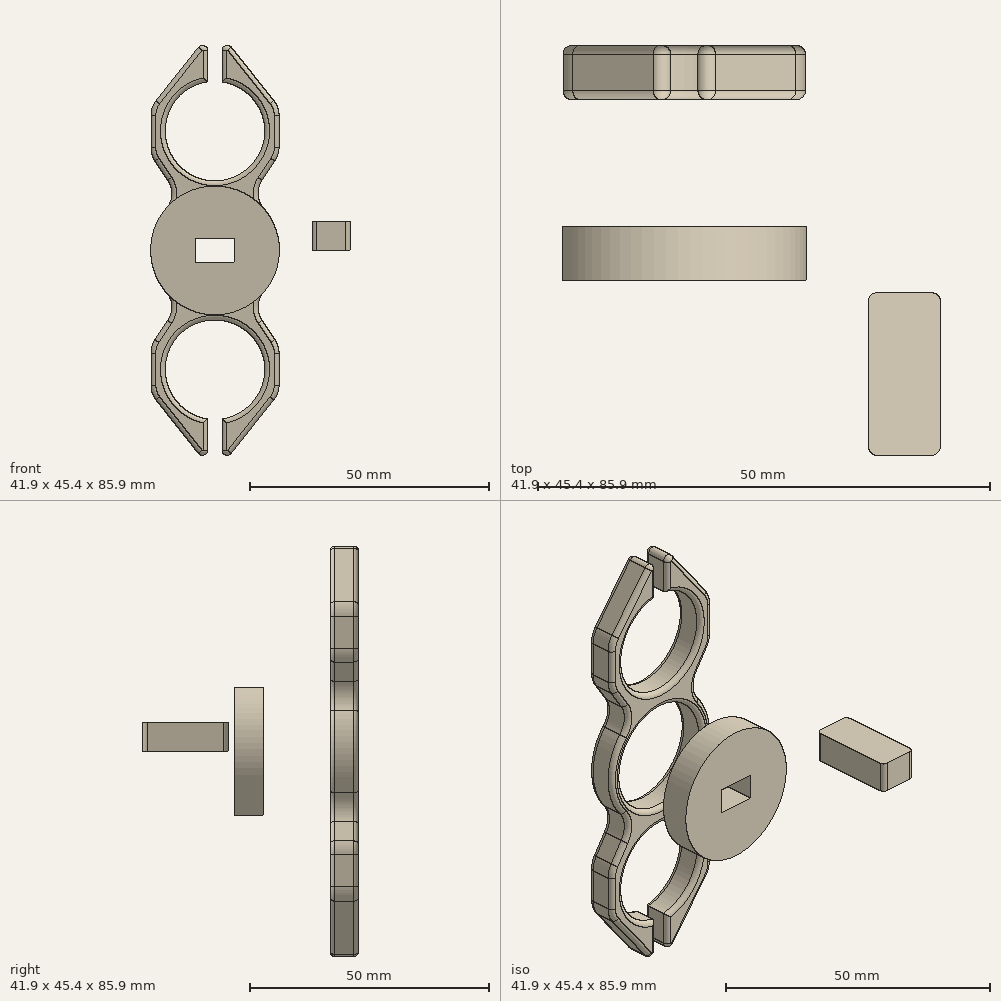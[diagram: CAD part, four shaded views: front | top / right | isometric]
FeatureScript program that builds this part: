
annotation { "Feature Type Name" : "Feature", "Feature Type Description" : "" }
export const myFeature = defineFeature(function(context is Context, id is Id, definition is map)
    precondition{}
    {
        {
            var Q0;
            Q0=qCreatedBy(makeId("Front.planeOp"),FACE);
            var sketch = newSketch(context, id + "F0", { "sketchPlane" : qUnion([Q0])});
            skCircle(sketch, "E0", {"center": v(0, 0) * mm, "radius": 10.93 * mm});
            skLineSegment(sketch, "E1", {"start": v(0, 0) * mm, "end": v(0, 25) * mm, "construction": true});
            skArc(sketch, "E2", {"start": v(-1.5, 35.32) * mm, "mid": v(0, 14.58) * mm, "end": v(1.5, 35.32) * mm});
            skArc(sketch, "E3.1.0", {"start": v(1.5, -35.32) * mm, "mid": v(0, -14.58) * mm, "end": v(-1.5, -35.32) * mm});
            skLineSegment(sketch, "E4.left", {"start": v(1.5, -41.86) * mm, "end": v(1.5, -35.32) * mm});
            skLineSegment(sketch, "E4.right", {"start": v(-1.5, -41.86) * mm, "end": v(-1.5, -35.32) * mm});
            skLineSegment(sketch, "E5.left", {"start": v(13.42, -28.26) * mm, "end": v(13.42, -21.51) * mm});
            skLineSegment(sketch, "E5.right", {"start": v(-13.42, -28.26) * mm, "end": v(-13.42, -21.51) * mm});
            skLineSegment(sketch, "E6.left", {"start": v(13.42, 21.51) * mm, "end": v(13.42, 28.26) * mm});
            skLineSegment(sketch, "E6.right", {"start": v(-13.42, 21.51) * mm, "end": v(-13.42, 28.26) * mm});
            skLineSegment(sketch, "E7", {"start": v(12.33, 31.37) * mm, "end": v(3.45, 42.54) * mm});
            skLineSegment(sketch, "E8", {"start": v(-3.45, 42.54) * mm, "end": v(-12.33, 31.37) * mm});
            skArc(sketch, "E9", {"start": v(10.23, -8.68) * mm, "mid": v(13.42, 0) * mm, "end": v(10.23, 8.68) * mm});
            skLineSegment(sketch, "E10", {"start": v(12.33, -31.37) * mm, "end": v(3.45, -42.54) * mm});
            skLineSegment(sketch, "E11", {"start": v(-3.45, -42.54) * mm, "end": v(-12.33, -31.37) * mm});
            skLineSegment(sketch, "E12", {"start": v(12.58, -18.74) * mm, "end": v(9.88, -14.7) * mm});
            skLineSegment(sketch, "E13", {"start": v(-9.88, -14.7) * mm, "end": v(-12.58, -18.74) * mm});
            skLineSegment(sketch, "E14", {"start": v(12.58, 18.74) * mm, "end": v(9.88, 14.7) * mm});
            skLineSegment(sketch, "E15", {"start": v(-9.88, 14.7) * mm, "end": v(-12.58, 18.74) * mm});
            skLineSegment(sketch, "E16.trimOffspring", {"start": v(1.5, 35.32) * mm, "end": v(1.5, 41.86) * mm});
            skLineSegment(sketch, "E17.trimOffspring", {"start": v(-1.5, 35.32) * mm, "end": v(-1.5, 41.86) * mm});
            skArc(sketch, "E18.trimOffspring", {"start": v(-10.23, 8.68) * mm, "mid": v(-13.42, 0) * mm, "end": v(-10.23, -8.68) * mm});
            skPoint(sketch, "E19.visualSharp", {"position": v(13.42, 30) * mm});
            skArc(sketch, "E19.filletArc", {"start": v(13.42, 28.26) * mm, "mid": v(13.14, 29.9) * mm, "end": v(12.33, 31.37) * mm});
            skPoint(sketch, "E20.visualSharp", {"position": v(13.42, 20) * mm});
            skArc(sketch, "E20.filletArc", {"start": v(12.58, 18.74) * mm, "mid": v(13.2, 20.07) * mm, "end": v(13.42, 21.51) * mm});
            skPoint(sketch, "E21.visualSharp", {"position": v(-13.42, 20) * mm});
            skArc(sketch, "E21.filletArc", {"start": v(-13.42, 21.51) * mm, "mid": v(-13.2, 20.07) * mm, "end": v(-12.58, 18.74) * mm});
            skPoint(sketch, "E22.visualSharp", {"position": v(-13.42, 30) * mm});
            skArc(sketch, "E22.filletArc", {"start": v(-12.33, 31.37) * mm, "mid": v(-13.14, 29.9) * mm, "end": v(-13.42, 28.26) * mm});
            skPoint(sketch, "E23.visualSharp", {"position": v(-1.5, 45) * mm});
            skArc(sketch, "E23.filletArc", {"start": v(-1.5, 41.86) * mm, "mid": v(-2.23, 42.9) * mm, "end": v(-3.45, 42.54) * mm});
            skPoint(sketch, "E24.visualSharp", {"position": v(1.5, 45) * mm});
            skArc(sketch, "E24.filletArc", {"start": v(3.45, 42.54) * mm, "mid": v(2.23, 42.9) * mm, "end": v(1.5, 41.86) * mm});
            skPoint(sketch, "E25.visualSharp", {"position": v(13.42, -20) * mm});
            skArc(sketch, "E25.filletArc", {"start": v(13.42, -21.51) * mm, "mid": v(13.2, -20.07) * mm, "end": v(12.58, -18.74) * mm});
            skPoint(sketch, "E26.visualSharp", {"position": v(13.42, -30) * mm});
            skArc(sketch, "E26.filletArc", {"start": v(12.33, -31.37) * mm, "mid": v(13.14, -29.9) * mm, "end": v(13.42, -28.26) * mm});
            skPoint(sketch, "E27.visualSharp", {"position": v(1.5, -45) * mm});
            skArc(sketch, "E27.filletArc", {"start": v(1.5, -41.86) * mm, "mid": v(2.23, -42.9) * mm, "end": v(3.45, -42.54) * mm});
            skPoint(sketch, "E28.visualSharp", {"position": v(-1.5, -45) * mm});
            skArc(sketch, "E28.filletArc", {"start": v(-3.45, -42.54) * mm, "mid": v(-2.23, -42.9) * mm, "end": v(-1.5, -41.86) * mm});
            skPoint(sketch, "E29.visualSharp", {"position": v(-13.42, -30) * mm});
            skArc(sketch, "E29.filletArc", {"start": v(-13.42, -28.26) * mm, "mid": v(-13.14, -29.9) * mm, "end": v(-12.33, -31.37) * mm});
            skPoint(sketch, "E30.visualSharp", {"position": v(-13.42, -20) * mm});
            skArc(sketch, "E30.filletArc", {"start": v(-12.58, -18.74) * mm, "mid": v(-13.2, -20.07) * mm, "end": v(-13.42, -21.51) * mm});
            skPoint(sketch, "E31.visualSharp", {"position": v(7.5, -11.13) * mm});
            skArc(sketch, "E31.filletArc", {"start": v(10.23, -8.68) * mm, "mid": v(9.05, -11.63) * mm, "end": v(9.88, -14.7) * mm});
            skPoint(sketch, "E32.visualSharp", {"position": v(-7.5, -11.13) * mm});
            skArc(sketch, "E32.filletArc", {"start": v(-9.88, -14.7) * mm, "mid": v(-9.05, -11.63) * mm, "end": v(-10.23, -8.68) * mm});
            skPoint(sketch, "E33.visualSharp", {"position": v(7.5, 11.13) * mm});
            skArc(sketch, "E33.filletArc", {"start": v(9.88, 14.7) * mm, "mid": v(9.05, 11.63) * mm, "end": v(10.23, 8.68) * mm});
            skPoint(sketch, "E34.visualSharp", {"position": v(-7.5, 11.13) * mm});
            skArc(sketch, "E34.filletArc", {"start": v(-10.23, 8.68) * mm, "mid": v(-9.05, 11.63) * mm, "end": v(-9.88, 14.7) * mm});
            skSolve(sketch);
        }
        {
            var Q0;
            Q0=makeQuery(id+"F0.imprint","IMPRINT",FACE,{"disambiguationData":[TD([[makeQuery(id+"F0.imprint","IMPRINT",EDGE,{"derivedFrom":sQuery(id+"F0.wireOp",EDGE,"E0")}),-1.0]])]});
            extrude(context, id + "F1", {"entities" : qUnion([Q0]), "depth" : 6 * mm, "offsetDistance" : 25 * mm});
        }
        {
            var Q0;
            Q0=makeQuery(id+"F1.opExtrude","CAP_FACE",FACE,{"disambiguationData":[OSD([sQuery(id+"F0.wireOp",EDGE,"E0"),sQuery(id+"F0.wireOp",EDGE,"E2"),sQuery(id+"F0.wireOp",EDGE,"E3.1.0"),sQuery(id+"F0.wireOp",EDGE,"E3.2.0"),sQuery(id+"F0.wireOp",EDGE,"E3.3.0"),sQuery(id+"F0.wireOp",EDGE,"E3.4.0"),sQuery(id+"F0.wireOp",EDGE,"6w4LuyIg-Judz-7qcx-iNhM-kCVs0XRHMAQz.left"),sQuery(id+"F0.wireOp",EDGE,"6w4LuyIg-Judz-7qcx-iNhM-kCVs0XRHMAQz.right"),sQuery(id+"F0.wireOp",EDGE,"GuxD1Two-tXSI-jhGi-diOq-QsG6SmieNdRW"),sQuery(id+"F0.wireOp",EDGE,"9e989a9f-be13-4d0f-822f-95c7c0624428.1.0"),sQuery(id+"F0.wireOp",EDGE,"9e989a9f-be13-4d0f-822f-95c7c0624428.1.1"),sQuery(id+"F0.wireOp",EDGE,"9e989a9f-be13-4d0f-822f-95c7c0624428.1.2"),sQuery(id+"F0.wireOp",EDGE,"9e989a9f-be13-4d0f-822f-95c7c0624428.2.0"),sQuery(id+"F0.wireOp",EDGE,"9e989a9f-be13-4d0f-822f-95c7c0624428.2.1"),sQuery(id+"F0.wireOp",EDGE,"9e989a9f-be13-4d0f-822f-95c7c0624428.2.2"),sQuery(id+"F0.wireOp",EDGE,"9e989a9f-be13-4d0f-822f-95c7c0624428.3.0"),sQuery(id+"F0.wireOp",EDGE,"9e989a9f-be13-4d0f-822f-95c7c0624428.3.1"),sQuery(id+"F0.wireOp",EDGE,"9e989a9f-be13-4d0f-822f-95c7c0624428.3.2"),sQuery(id+"F0.wireOp",EDGE,"9e989a9f-be13-4d0f-822f-95c7c0624428.4.0"),sQuery(id+"F0.wireOp",EDGE,"9e989a9f-be13-4d0f-822f-95c7c0624428.4.1"),sQuery(id+"F0.wireOp",EDGE,"9e989a9f-be13-4d0f-822f-95c7c0624428.4.2"),sQuery(id+"F0.wireOp",EDGE,"486a15bc-75c9-41d0-808c-e5c4775e6e80.filletArc"),sQuery(id+"F0.wireOp",EDGE,"d314a861-2769-46d2-9bec-117903992242.filletArc"),sQuery(id+"F0.wireOp",EDGE,"5d220be9-c9be-4508-b7a3-f434c5fdea58.filletArc"),sQuery(id+"F0.wireOp",EDGE,"2974d6c2-e4a2-45df-9bc2-224e587c2884.filletArc"),sQuery(id+"F0.wireOp",EDGE,"3265ed39-f9f2-4246-9e43-8a9d8c4dec78.filletArc")])],"isStart":false});
            var Q1;
            Q1=makeQuery(id+"F1.opExtrude","CAP_FACE",FACE,{"disambiguationData":[OSD([sQuery(id+"F0.wireOp",EDGE,"E0"),sQuery(id+"F0.wireOp",EDGE,"E2"),sQuery(id+"F0.wireOp",EDGE,"E3.1.0"),sQuery(id+"F0.wireOp",EDGE,"E3.2.0"),sQuery(id+"F0.wireOp",EDGE,"E3.3.0"),sQuery(id+"F0.wireOp",EDGE,"E3.4.0"),sQuery(id+"F0.wireOp",EDGE,"6w4LuyIg-Judz-7qcx-iNhM-kCVs0XRHMAQz.left"),sQuery(id+"F0.wireOp",EDGE,"6w4LuyIg-Judz-7qcx-iNhM-kCVs0XRHMAQz.right"),sQuery(id+"F0.wireOp",EDGE,"GuxD1Two-tXSI-jhGi-diOq-QsG6SmieNdRW"),sQuery(id+"F0.wireOp",EDGE,"9e989a9f-be13-4d0f-822f-95c7c0624428.1.0"),sQuery(id+"F0.wireOp",EDGE,"9e989a9f-be13-4d0f-822f-95c7c0624428.1.1"),sQuery(id+"F0.wireOp",EDGE,"9e989a9f-be13-4d0f-822f-95c7c0624428.1.2"),sQuery(id+"F0.wireOp",EDGE,"9e989a9f-be13-4d0f-822f-95c7c0624428.2.0"),sQuery(id+"F0.wireOp",EDGE,"9e989a9f-be13-4d0f-822f-95c7c0624428.2.1"),sQuery(id+"F0.wireOp",EDGE,"9e989a9f-be13-4d0f-822f-95c7c0624428.2.2"),sQuery(id+"F0.wireOp",EDGE,"9e989a9f-be13-4d0f-822f-95c7c0624428.3.0"),sQuery(id+"F0.wireOp",EDGE,"9e989a9f-be13-4d0f-822f-95c7c0624428.3.1"),sQuery(id+"F0.wireOp",EDGE,"9e989a9f-be13-4d0f-822f-95c7c0624428.3.2"),sQuery(id+"F0.wireOp",EDGE,"9e989a9f-be13-4d0f-822f-95c7c0624428.4.0"),sQuery(id+"F0.wireOp",EDGE,"9e989a9f-be13-4d0f-822f-95c7c0624428.4.1"),sQuery(id+"F0.wireOp",EDGE,"9e989a9f-be13-4d0f-822f-95c7c0624428.4.2"),sQuery(id+"F0.wireOp",EDGE,"486a15bc-75c9-41d0-808c-e5c4775e6e80.filletArc"),sQuery(id+"F0.wireOp",EDGE,"d314a861-2769-46d2-9bec-117903992242.filletArc"),sQuery(id+"F0.wireOp",EDGE,"5d220be9-c9be-4508-b7a3-f434c5fdea58.filletArc"),sQuery(id+"F0.wireOp",EDGE,"2974d6c2-e4a2-45df-9bc2-224e587c2884.filletArc"),sQuery(id+"F0.wireOp",EDGE,"3265ed39-f9f2-4246-9e43-8a9d8c4dec78.filletArc")])],"isStart":true});
            fillet(context, id + "F2", {"entities" : qUnion([Q0, Q1]), "radius" : 1 * mm, "tangentPropagation" : true, "allowEdgeOverflow" : false});
        }
        {
            var Q0;
            Q0=qCreatedBy(makeId("Top.planeOp"),FACE);
            var sketch = newSketch(context, id + "F3", { "sketchPlane" : qUnion([Q0])});
            skLineSegment(sketch, "E35.bottom", {"start": v(21.35, -27.36) * mm, "end": v(27.35, -27.36) * mm});
            skLineSegment(sketch, "E35.top", {"start": v(21.35, -45.36) * mm, "end": v(27.35, -45.36) * mm});
            skLineSegment(sketch, "E35.left", {"start": v(20.35, -28.36) * mm, "end": v(20.35, -44.36) * mm});
            skLineSegment(sketch, "E35.right", {"start": v(28.35, -28.36) * mm, "end": v(28.35, -44.36) * mm});
            skPoint(sketch, "E35.middle", {"position": v(24.35, -36.36) * mm});
            skPoint(sketch, "E36.visualSharp", {"position": v(20.35, -45.36) * mm});
            skArc(sketch, "E36.filletArc", {"start": v(20.35, -44.36) * mm, "mid": v(20.64, -45.06) * mm, "end": v(21.35, -45.36) * mm});
            skPoint(sketch, "E37.visualSharp", {"position": v(28.35, -45.36) * mm});
            skArc(sketch, "E37.filletArc", {"start": v(27.35, -45.36) * mm, "mid": v(28.05, -45.06) * mm, "end": v(28.35, -44.36) * mm});
            skPoint(sketch, "E38.visualSharp", {"position": v(28.35, -27.36) * mm});
            skArc(sketch, "E38.filletArc", {"start": v(28.35, -28.36) * mm, "mid": v(28.05, -27.65) * mm, "end": v(27.35, -27.36) * mm});
            skPoint(sketch, "E39.visualSharp", {"position": v(20.35, -27.36) * mm});
            skArc(sketch, "E39.filletArc", {"start": v(21.35, -27.36) * mm, "mid": v(20.64, -27.65) * mm, "end": v(20.35, -28.36) * mm});
            skSolve(sketch);
        }
        {
            var Q0;
            Q0=makeQuery(id+"F3.imprint","IMPRINT",FACE,{"disambiguationData":[TD([[makeQuery(id+"F3.imprint","IMPRINT",EDGE,{"derivedFrom":sQuery(id+"F3.wireOp",EDGE,"E35.bottom")}),-1.0]])]});
            extrude(context, id + "F4", {"entities" : qUnion([Q0]), "depth" : 6 * mm, "offsetDistance" : 25 * mm});
        }
        {
            var Q0;
            Q0=qCreatedBy(makeId("Front.planeOp"),FACE);
            var sketch = newSketch(context, id + "F5", { "sketchPlane" : qUnion([Q0])});
            skCircle(sketch, "E40", {"center": v(0, 0) * mm, "radius": 13.5 * mm});
            skLineSegment(sketch, "E41.bottom", {"start": v(4, -2.5) * mm, "end": v(-4, -2.5) * mm});
            skLineSegment(sketch, "E41.top", {"start": v(4, 2.5) * mm, "end": v(-4, 2.5) * mm});
            skLineSegment(sketch, "E41.left", {"start": v(4, -2.5) * mm, "end": v(4, 2.5) * mm});
            skLineSegment(sketch, "E41.right", {"start": v(-4, -2.5) * mm, "end": v(-4, 2.5) * mm});
            skSolve(sketch);
        }
        {
            var Q0;
            Q0=qSketchRegion(id+"F5",true);
            extrude(context, id + "F6", {"entities" : qUnion([Q0]), "depth" : 26 * mm, "offsetDistance" : 25 * mm, "hasSecondDirection" : true, "secondDirectionOppositeDirection" : false, "secondDirectionDepth" : 20 * mm});
        }
    });
